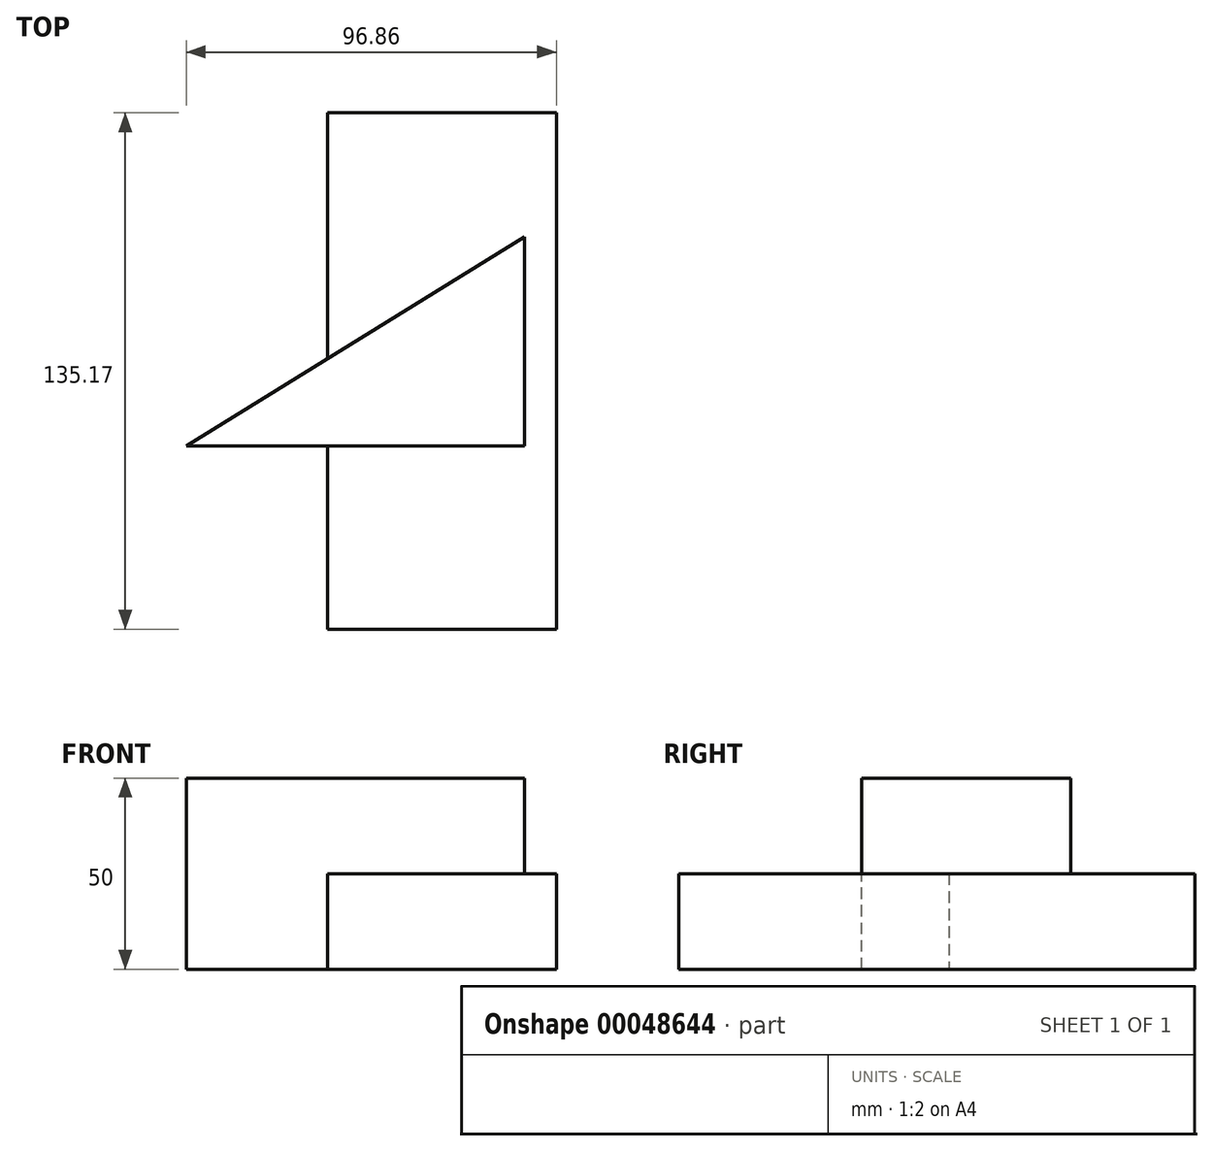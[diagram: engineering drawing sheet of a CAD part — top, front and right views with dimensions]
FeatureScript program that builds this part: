
annotation { "Feature Type Name" : "Feature", "Feature Type Description" : "" }
export const myFeature = defineFeature(function(context is Context, id is Id, definition is map)
    precondition{}
    {
        {
            var Q0;
            Q0=qCreatedBy(makeId("Top.planeOp"),FACE);
            var sketch = newSketch(context, id + "F0", { "sketchPlane" : qUnion([Q0])});
            skLineSegment(sketch, "E0", {"start": v(-51.23, -34.81) * mm, "end": v(37.27, -34.81) * mm});
            skLineSegment(sketch, "E1", {"start": v(37.27, -34.81) * mm, "end": v(37.27, 19.9) * mm});
            skLineSegment(sketch, "E2", {"start": v(37.27, 19.9) * mm, "end": v(-51.23, -34.81) * mm});
            skSolve(sketch);
        }
        {
            var Q0;
            Q0 = qSketchRegion(id + "F0", true);
            extrude(context, id + "F1", {"entities" : qUnion([Q0]), "depth" : 50 * mm});
        }
        {
            var Q0;
            Q0=qCreatedBy(makeId("Top.planeOp"),FACE);
            var sketch = newSketch(context, id + "F2", { "sketchPlane" : qUnion([Q0])});
            skLineSegment(sketch, "E3.bottom", {"start": v(62.69, -82.76) * mm, "end": v(62.7, -82.76) * mm});
            skLineSegment(sketch, "E3.top", {"start": v(62.69, -70.76) * mm, "end": v(62.7, -70.76) * mm});
            skLineSegment(sketch, "E3.left", {"start": v(62.69, -82.76) * mm, "end": v(62.69, -70.76) * mm});
            skLineSegment(sketch, "E3.right", {"start": v(62.7, -82.76) * mm, "end": v(62.7, -70.76) * mm});
            skLineSegment(sketch, "E4.bottom", {"start": v(-14.31, -82.76) * mm, "end": v(45.63, -82.76) * mm});
            skLineSegment(sketch, "E4.top", {"start": v(-14.31, 52.41) * mm, "end": v(45.63, 52.41) * mm});
            skLineSegment(sketch, "E4.left", {"start": v(-14.31, -82.76) * mm, "end": v(-14.31, 52.41) * mm});
            skLineSegment(sketch, "E4.right", {"start": v(45.63, -82.76) * mm, "end": v(45.63, 52.41) * mm});
            skSolve(sketch);
        }
        {
            var Q0;
            Q0=makeQuery(id+"F2.imprint","IMPRINT",FACE,{"disambiguationData":[TD([[makeQuery(id+"F2.imprint","IMPRINT",EDGE,{"derivedFrom":sQuery(id+"F2.wireOp",EDGE,"E4.bottom")}),1.0]])]});
            extrude(context, id + "F3", {"entities" : qUnion([Q0]), "operationType" : NewBodyOperationType.ADD, "depth" : 25 * mm});
        }
    });
